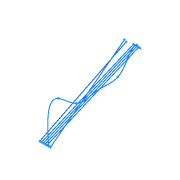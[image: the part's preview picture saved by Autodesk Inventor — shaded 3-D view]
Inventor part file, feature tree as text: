
AUTODESK INVENTOR PART (.ipt)
format: ipt  version: 2016 (Build 200138000, 138)  size: 509,440 bytes
history: native  units: mm (DEFAULTED — no unit token found)
features: other x40, plane x9, sketch x9, sweep x9
ambient origin geometry x8: Origin, YZ Plane, XZ Plane, XY Plane, X Axis, Y Axis, Z Axis, Center Point
bodies: Body1 (feature_tree), Body2 (feature_tree), Body3 (feature_tree), Body4 (feature_tree), Body5 (feature_tree), Body6 (feature_tree), Body7 (feature_tree), Body8 (feature_tree), Body9 (feature_tree)
feature tree (67):
  other  "Work Point15"
  other  "Work Point37"
  other  "Work Point54"
  other  "Work Point55"
  other  "Wire8"
  other  "Work Point56"
  other  "Work Point57"
  other  "Wire9"
  other  "Work Point58"
  other  "Work Point59"
  other  "Wire10"
  other  "Work Point60"
  other  "Work Point61"
  other  "Wire11"
  other  "Work Point78"
  other  "Work Point79"
  other  "Segment2"
  plane  "Work Plane88"
  plane  "Work Plane90"
  plane  "Work Plane91"
  plane  "Work Plane92"
  plane  "Work Plane93"
  plane  "Work Plane95"
  plane  "Work Plane96"
  plane  "Work Plane97"
  plane  "Work Plane98"
  other  "Work Point80"
  other  "Work Point81"
  other  "Work Point82"
  other  "Work Point83"
  other  "Work Point84"
  other  "Work Point85"
  other  "Work Point86"
  other  "Work Point87"
  other  "Work Point88"
  other  "Work Point89"
  other  "Work Point90"
  other  "Work Point91"
  other  "Work Point92"
  other  "Work Point93"
  sketch  "Sketch88"  dims[d174=0.0mm d175=0.0mm d178=0.0mm d179=0.0mm]
  other  "Srf88"
  sketch  "Sketch90"  dims[d180=0.0mm d181=0.0mm d182=0.0mm d183=0.0mm]
  other  "Srf90"
  sketch  "Sketch91"  dims[d184=0.0mm d185=0.0mm d188=0.0mm d189=0.0mm]
  other  "Srf91"
  sketch  "Sketch92"  dims[d190=0.0mm d191=0.0mm d192=0.0mm d193=0.0mm]
  other  "Srf92"
  sketch  "Sketch93"  dims[d194=0.0mm d195=0.0mm]
  other  "Srf93"
  sketch  "Sketch95"
  other  "Srf95"
  sketch  "Sketch96"
  other  "Srf96"
  sketch  "Sketch97"
  other  "Srf97"
  sketch  "Sketch98"
  other  "Srf98"
  sweep  "SweepSrf88"
  sweep  "SweepSrf90"
  sweep  "SweepSrf91"
  sweep  "SweepSrf92"
  sweep  "SweepSrf93"
  sweep  "SweepSrf95"
  sweep  "SweepSrf96"
  sweep  "SweepSrf97"
  sweep  "SweepSrf98"
